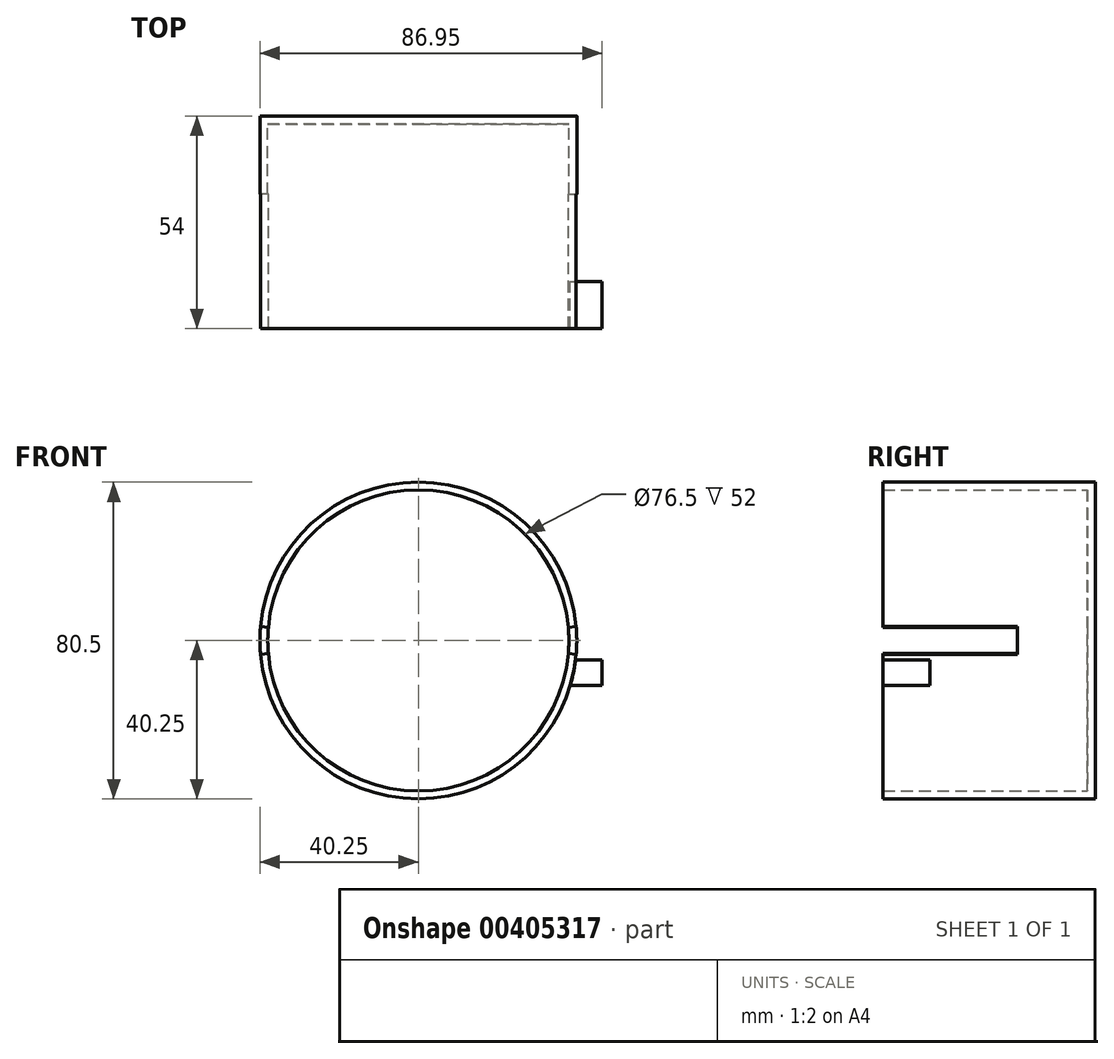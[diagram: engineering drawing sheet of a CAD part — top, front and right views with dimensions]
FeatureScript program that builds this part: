
annotation { "Feature Type Name" : "Feature", "Feature Type Description" : "" }
export const myFeature = defineFeature(function(context is Context, id is Id, definition is map)
    precondition{}
    {
        {
            var Q0;
            Q0=qCreatedBy(makeId("Front.planeOp"),FACE);
            var sketch = newSketch(context, id + "F0", { "sketchPlane" : qUnion([Q0])});
            skCircle(sketch, "E0", {"center": v(0, 0) * mm, "radius": 40.25 * mm});
            skSolve(sketch);
        }
        {
            var Q0;
            Q0=makeQuery(id+"F0.imprint","IMPRINT",FACE,{"disambiguationData":[TD([[makeQuery(id+"F0.imprint","IMPRINT",EDGE,{"derivedFrom":sQuery(id+"F0.wireOp",EDGE,"E0")}),1.0]])]});
            extrude(context, id + "F1", {"entities" : qUnion([Q0]), "depth" : 54 * mm});
        }
        {
            var Q0;
            Q0=makeQuery(id+"F1.opExtrude","CAP_FACE",FACE,{"disambiguationData":[OSD([sQuery(id+"F0.wireOp",EDGE,"E0")])],"isStart":false});
            shell(context, id + "F2", {"entities" : qUnion([Q0]), "thickness" : 2 * mm});
        }
        {
            var Q0;
            Q0=qCreatedBy(makeId("Top.planeOp"),FACE);
            var sketch = newSketch(context, id + "F3", { "sketchPlane" : qUnion([Q0])});
            skLineSegment(sketch, "E1.bottom", {"start": v(-37.7, -19.85) * mm, "end": v(-43.95, -19.85) * mm});
            skLineSegment(sketch, "E1.top", {"start": v(-37.7, -54.85) * mm, "end": v(-43.95, -54.85) * mm});
            skLineSegment(sketch, "E1.left", {"start": v(-37.7, -19.85) * mm, "end": v(-37.7, -54.85) * mm});
            skLineSegment(sketch, "E1.right", {"start": v(-43.95, -19.85) * mm, "end": v(-43.95, -54.85) * mm});
            skLineSegment(sketch, "E2.bottom", {"start": v(37.67, -19.85) * mm, "end": v(44.23, -19.85) * mm});
            skLineSegment(sketch, "E2.top", {"start": v(37.67, -54.85) * mm, "end": v(44.23, -54.85) * mm});
            skLineSegment(sketch, "E2.left", {"start": v(37.67, -19.85) * mm, "end": v(37.67, -54.85) * mm});
            skLineSegment(sketch, "E2.right", {"start": v(44.23, -19.85) * mm, "end": v(44.23, -54.85) * mm});
            skSolve(sketch);
        }
        {
            var Q0;
            Q0=makeQuery(id+"F3.imprint","IMPRINT",FACE,{"disambiguationData":[TD([[makeQuery(id+"F3.imprint","IMPRINT",EDGE,{"derivedFrom":sQuery(id+"F3.wireOp",EDGE,"E2.bottom")}),-1.0]])]});
            var Q1;
            Q1=makeQuery(id+"F3.imprint","IMPRINT",FACE,{"disambiguationData":[TD([[makeQuery(id+"F3.imprint","IMPRINT",EDGE,{"derivedFrom":sQuery(id+"F3.wireOp",EDGE,"E1.bottom")}),1.0]])]});
            var Q2;
            Q2=makeQuery(id+"F1.opExtrude","CAP_EDGE",EDGE,{"disambiguationData":[OSD([sQuery(id+"F0.wireOp",EDGE,"E0")])],"isStart":true});
            revolve(context, id + "F4", {"operationType" : NewBodyOperationType.REMOVE, "entities" : qUnion([Q0, Q1]), "axis" : qUnion([Q2]), "revolveType" : RevolveType.SYMMETRIC, "angle" : 10 * degree});
        }
        {
            var Q0;
            Q0=qCreatedBy(makeId("Front.planeOp"),FACE);
            var sketch = newSketch(context, id + "F5", { "sketchPlane" : qUnion([Q0])});
            skLineSegment(sketch, "E3.bottom", {"start": v(39.95, -4.9) * mm, "end": v(46.7, -4.9) * mm});
            skLineSegment(sketch, "E3.top", {"start": v(38.58, -11.46) * mm, "end": v(46.7, -11.46) * mm});
            skLineSegment(sketch, "E3.right", {"start": v(46.7, -4.9) * mm, "end": v(46.7, -11.46) * mm});
            skArc(sketch, "E4", {"start": v(38.58, -11.46) * mm, "mid": v(39.4, -8.2) * mm, "end": v(39.95, -4.9) * mm});
            skSolve(sketch);
        }
        {
            var Q0;
            Q0=makeQuery(id+"F5.imprint","IMPRINT",FACE,{"disambiguationData":[TD([[makeQuery(id+"F5.imprint","IMPRINT",EDGE,{"derivedFrom":sQuery(id+"F5.wireOp",EDGE,"E3.bottom")}),-1.0]])]});
            extrude(context, id + "F6", {"entities" : qUnion([Q0]), "depth" : 12 * mm});
        }
        {
            var Q0;
            Q0=makeQuery(id+"F6.opExtrude","SWEPT_BODY",BODY,{"disambiguationData":[OSD([sQuery(id+"F5.wireOp",EDGE,"E3.bottom"),sQuery(id+"F5.wireOp",EDGE,"E3.top"),sQuery(id+"F5.wireOp",EDGE,"E3.right"),sQuery(id+"F5.wireOp",EDGE,"E4")])]});
            transform(context, id + "F7", {"entities" : qUnion([Q0]), "transformType" : TransformType.TRANSLATION_3D, "dx" : 0 * mm, "dy" : -42 * mm, "dz" : 0 * mm, "makeCopy" : false});
        }
    });
